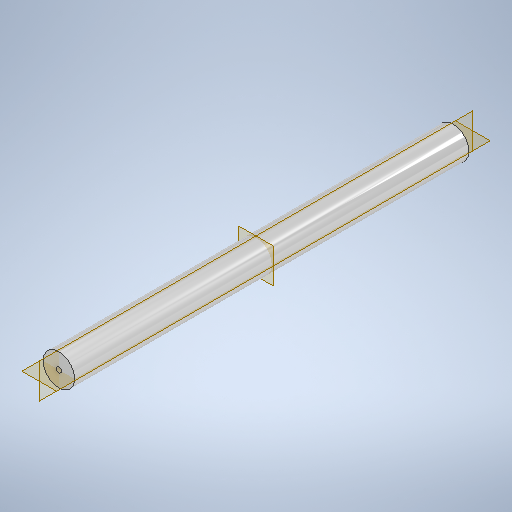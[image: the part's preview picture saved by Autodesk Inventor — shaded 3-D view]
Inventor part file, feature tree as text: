
AUTODESK INVENTOR PART (.ipt)
format: ipt  version: 2025.2 (Build 292293000, 293)  size: 258,560 bytes
history: native  units: mm
features: sketch x2, extrude x1
ambient origin geometry x8: Origin, YZ Plane, XZ Plane, XY Plane, X Axis, Y Axis, Z Axis, Center Point
bodies: Solid1 (feature_tree)
feature tree (3):
  extrude  "Extrusion1"  Depth=25.0mm
  sketch  "Sketch2"  dims[d2=750.0mm d3=0.0mm]
  sketch  "Sketch1"  dims[d0=60.0mm d1=25.0mm]
